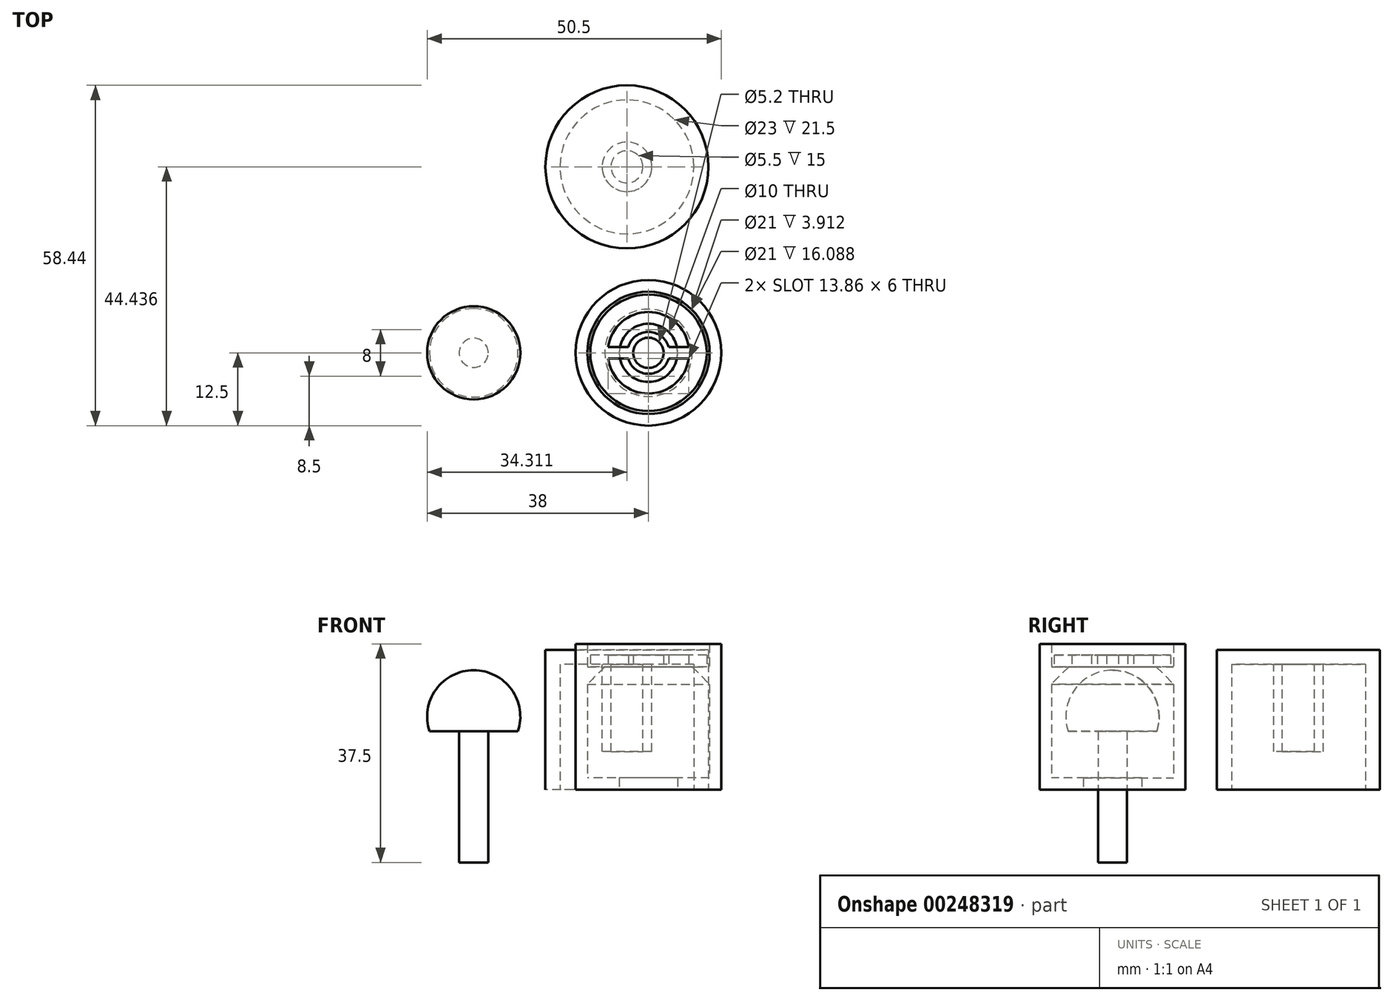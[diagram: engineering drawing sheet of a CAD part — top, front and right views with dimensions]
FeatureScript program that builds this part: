
annotation { "Feature Type Name" : "Feature", "Feature Type Description" : "" }
export const myFeature = defineFeature(function(context is Context, id is Id, definition is map)
    precondition{}
    {
        {
            var Q0;
            Q0=qCreatedBy(makeId("Top.planeOp"),FACE);
            var sketch = newSketch(context, id + "F0", { "sketchPlane" : qUnion([Q0])});
            skCircle(sketch, "E0", {"center": v(0, 0) * mm, "radius": 2.5 * mm});
            skSolve(sketch);
        }
        {
            var Q0;
            Q0=makeQuery(id+"F0.imprint","IMPRINT",FACE,{"disambiguationData":[TD([[makeQuery(id+"F0.imprint","IMPRINT",EDGE,{"derivedFrom":sQuery(id+"F0.wireOp",EDGE,"E0")}),1.0]])]});
            extrude(context, id + "F1", {"entities" : qUnion([Q0]), "endBound" : BoundingType.SYMMETRIC, "depth" : 25 * mm});
        }
        {
            var Q0;
            Q0=qCreatedBy(makeId("Right.planeOp"),FACE);
            var sketch = newSketch(context, id + "F2", { "sketchPlane" : qUnion([Q0])});
            skArc(sketch, "E1", {"start": v(7.6, 10) * mm, "mid": v(0, 20.5) * mm, "end": v(-7.6, 10) * mm});
            skLineSegment(sketch, "E2", {"start": v(7.6, 10) * mm, "end": v(-7.6, 10) * mm});
            skLineSegment(sketch, "E3", {"start": v(0, 10) * mm, "end": v(0, 20.5) * mm});
            skSolve(sketch);
        }
        {
            var Q0;
            {var subQ3=sQuery(id+"F2.wireOp",EDGE,"E3");Q0=makeQuery(id+"F2.imprint","IMPRINT",FACE,{"disambiguationData":[TD([[makeQuery(id+"F2.imprint","IMPRINT",EDGE,{"derivedFrom":subQ3}),-1.0]])]});}
            var Q1;
            Q1=sQuery(id+"F2.wireOp",EDGE,"E3");
            revolve(context, id + "F3", {"operationType" : NewBodyOperationType.ADD, "entities" : qUnion([Q0]), "axis" : qUnion([Q1]), "revolveType" : RevolveType.FULL});
        }
        {
            var Q0;
            Q0=qCreatedBy(makeId("Top.planeOp"),FACE);
            var sketch = newSketch(context, id + "F4", { "sketchPlane" : qUnion([Q0])});
            skCircle(sketch, "E4", {"center": v(30, 0) * mm, "radius": 5 * mm});
            skCircle(sketch, "E5", {"center": v(30, 0) * mm, "radius": 12.5 * mm});
            skSolve(sketch);
        }
        {
            var Q0;
            Q0=makeQuery(id+"F4.imprint","IMPRINT",FACE,{"disambiguationData":[TD([[makeQuery(id+"F4.imprint","IMPRINT",EDGE,{"derivedFrom":sQuery(id+"F4.wireOp",EDGE,"E4")}),-1.0]])]});
            extrude(context, id + "F5", {"entities" : qUnion([Q0]), "depth" : 2 * mm});
        }
        {
            var Q0;
            Q0=qCreatedBy(makeId("Front.planeOp"),FACE);
            var sketch = newSketch(context, id + "F6", { "sketchPlane" : qUnion([Q0])});
            skLineSegment(sketch, "E6.bottom", {"start": v(40.5, 0) * mm, "end": v(42.5, 0) * mm});
            skLineSegment(sketch, "E6.top", {"start": v(40.5, 25) * mm, "end": v(42.5, 25) * mm});
            skLineSegment(sketch, "E6.left", {"start": v(42.5, 0) * mm, "end": v(42.5, 25) * mm});
            skLineSegment(sketch, "E6.right", {"start": v(40.5, 0) * mm, "end": v(40.5, 25) * mm});
            skLineSegment(sketch, "E7", {"start": v(40.5, 18.09) * mm, "end": v(37.5, 21.09) * mm});
            skLineSegment(sketch, "E8", {"start": v(37.5, 21.09) * mm, "end": v(40.5, 21.09) * mm});
            skLineSegment(sketch, "E9", {"start": v(30, 0) * mm, "end": v(30, 27.95) * mm});
            skSolve(sketch);
        }
        {
            var Q0;
            {var subQ1=sQuery(id+"F6.wireOp",EDGE,"E6.bottom");Q0=makeQuery(id+"F6.imprint","IMPRINT",FACE,{"disambiguationData":[TD([[makeQuery(id+"F6.imprint","IMPRINT",EDGE,{"derivedFrom":subQ1}),1.0]])]});}
            var Q1;
            {var subQ0=sQuery(id+"F6.wireOp",EDGE,"E7");Q1=makeQuery(id+"F6.imprint","IMPRINT",FACE,{"disambiguationData":[TD([[makeQuery(id+"F6.imprint","IMPRINT",EDGE,{"derivedFrom":subQ0}),-1.0]])]});}
            var Q2;
            Q2=sQuery(id+"F6.wireOp",EDGE,"E9");
            revolve(context, id + "F7", {"operationType" : NewBodyOperationType.ADD, "entities" : qUnion([Q0, Q1]), "axis" : qUnion([Q2]), "revolveType" : RevolveType.FULL});
        }
        {
            var Q0;
            Q0=makeQuery(id+"F7.opRevolve","SWEPT_FACE",FACE,{"disambiguationData":[OSD([sQuery(id+"F6.wireOp",EDGE,"E8")])]});
            var sketch = newSketch(context, id + "F8", { "sketchPlane" : qUnion([Q0])});
            skCircle(sketch, "E10", {"center": v(30, 0) * mm, "radius": 7 * mm});
            skLineSegment(sketch, "E11", {"start": v(23.07, 1) * mm, "end": v(27.6, 1) * mm});
            skCircle(sketch, "E12", {"center": v(30, 0) * mm, "radius": 2.6 * mm});
            skCircle(sketch, "E13", {"center": v(30, 0) * mm, "radius": 3.6 * mm});
            skLineSegment(sketch, "E14", {"start": v(23, 0) * mm, "end": v(30, 0) * mm});
            skLineSegment(sketch, "E15.MirrorCS", {"start": v(23.07, -1) * mm, "end": v(27.6, -1) * mm});
            skLineSegment(sketch, "E16", {"start": v(30, 0) * mm, "end": v(30, 7) * mm});
            skLineSegment(sketch, "E17.MirrorCS", {"start": v(36.93, 1) * mm, "end": v(32.4, 1) * mm});
            skLineSegment(sketch, "E18.MirrorCS", {"start": v(36.93, -1) * mm, "end": v(32.4, -1) * mm});
            skCircle(sketch, "E19", {"center": v(30, 0) * mm, "radius": 10 * mm});
            skSolve(sketch);
        }
        {
            var Q0;
            {var subQ0=sQuery(id+"F8.wireOp",EDGE,"E12");var subQ1=sQuery(id+"F8.wireOp",EDGE,"E11");var subQ2=makeQuery(id+"F8.imprint","INTERSECT",VERTEX,{"derivedFrom":[subQ1,subQ0]});Q0=makeQuery(id+"F8.imprint","IMPRINT",FACE,{"disambiguationData":[TD([[makeQuery(id+"F8.imprint","IMPRINT",EDGE,{"disambiguationData":[TD([[subQ2,1.0]])],"derivedFrom":subQ1}),1.0]])]});}
            var Q1;
            {var subQ0=sQuery(id+"F8.wireOp",EDGE,"E17.MirrorCS");var subQ1=sQuery(id+"F8.wireOp",EDGE,"E12");var subQ2=makeQuery(id+"F8.imprint","INTERSECT",VERTEX,{"derivedFrom":[subQ1,subQ0]});Q1=makeQuery(id+"F8.imprint","IMPRINT",FACE,{"disambiguationData":[TD([[makeQuery(id+"F8.imprint","IMPRINT",EDGE,{"disambiguationData":[TD([[subQ2,-1.0]])],"derivedFrom":subQ1}),-1.0]])]});}
            var Q2;
            {var subQ0=sQuery(id+"F8.wireOp",EDGE,"E15.MirrorCS");var subQ1=sQuery(id+"F8.wireOp",EDGE,"E12");var subQ2=makeQuery(id+"F8.imprint","INTERSECT",VERTEX,{"derivedFrom":[subQ1,subQ0]});Q2=makeQuery(id+"F8.imprint","IMPRINT",FACE,{"disambiguationData":[TD([[makeQuery(id+"F8.imprint","IMPRINT",EDGE,{"disambiguationData":[TD([[subQ2,-1.0]])],"derivedFrom":subQ1}),-1.0]])]});}
            var Q3;
            {var subQ0=sQuery(id+"F8.wireOp",EDGE,"E17.MirrorCS");var subQ1=sQuery(id+"F8.wireOp",EDGE,"E12");var subQ2=makeQuery(id+"F8.imprint","INTERSECT",VERTEX,{"derivedFrom":[subQ1,subQ0]});Q3=makeQuery(id+"F8.imprint","IMPRINT",FACE,{"disambiguationData":[TD([[makeQuery(id+"F8.imprint","IMPRINT",EDGE,{"disambiguationData":[TD([[subQ2,1.0]])],"derivedFrom":subQ1}),-1.0]])]});}
            var Q4;
            {var subQ0=sQuery(id+"F8.wireOp",EDGE,"E14");var subQ1=sQuery(id+"F8.wireOp",EDGE,"E13");var subQ2=makeQuery(id+"F8.imprint","INTERSECT",VERTEX,{"derivedFrom":[subQ1,subQ0]});Q4=makeQuery(id+"F8.imprint","IMPRINT",FACE,{"disambiguationData":[TD([[makeQuery(id+"F8.imprint","IMPRINT",EDGE,{"disambiguationData":[TD([[subQ2,-1.0]])],"derivedFrom":subQ1}),-1.0]])]});}
            var Q5;
            {var subQ0=sQuery(id+"F8.wireOp",EDGE,"E13");var subQ1=sQuery(id+"F8.wireOp",EDGE,"E11");var subQ2=makeQuery(id+"F8.imprint","INTERSECT",VERTEX,{"derivedFrom":[subQ1,subQ0]});Q5=makeQuery(id+"F8.imprint","IMPRINT",FACE,{"disambiguationData":[TD([[makeQuery(id+"F8.imprint","IMPRINT",EDGE,{"disambiguationData":[TD([[subQ2,-1.0]])],"derivedFrom":subQ0}),-1.0]])]});}
            var Q6;
            {var subQ0=sQuery(id+"F8.wireOp",EDGE,"E12");var subQ1=sQuery(id+"F8.wireOp",EDGE,"E11");var subQ2=makeQuery(id+"F8.imprint","INTERSECT",VERTEX,{"derivedFrom":[subQ1,subQ0]});Q6=makeQuery(id+"F8.imprint","IMPRINT",FACE,{"disambiguationData":[TD([[makeQuery(id+"F8.imprint","IMPRINT",EDGE,{"disambiguationData":[TD([[subQ2,1.0]])],"derivedFrom":subQ1}),-1.0]])]});}
            var Q7;
            {var subQ0=sQuery(id+"F8.wireOp",EDGE,"E15.MirrorCS");var subQ1=sQuery(id+"F8.wireOp",EDGE,"E12");var subQ2=makeQuery(id+"F8.imprint","INTERSECT",VERTEX,{"derivedFrom":[subQ1,subQ0]});Q7=makeQuery(id+"F8.imprint","IMPRINT",FACE,{"disambiguationData":[TD([[makeQuery(id+"F8.imprint","IMPRINT",EDGE,{"disambiguationData":[TD([[subQ2,1.0]])],"derivedFrom":subQ1}),-1.0]])]});}
            var Q8;
            {var subQ0=sQuery(id+"F8.wireOp",EDGE,"E17.MirrorCS");var subQ1=sQuery(id+"F8.wireOp",EDGE,"E10");var subQ2=makeQuery(id+"F8.imprint","INTERSECT",VERTEX,{"derivedFrom":[subQ1,subQ0]});Q8=makeQuery(id+"F8.imprint","IMPRINT",FACE,{"disambiguationData":[TD([[makeQuery(id+"F8.imprint","IMPRINT",EDGE,{"disambiguationData":[TD([[subQ2,1.0]])],"derivedFrom":subQ1}),1.0]])]});}
            var Q9;
            {var subQ0=sQuery(id+"F8.wireOp",EDGE,"E14");var subQ1=sQuery(id+"F8.wireOp",EDGE,"E10");var subQ2=makeQuery(id+"F8.imprint","INTERSECT",VERTEX,{"derivedFrom":[subQ1,subQ0]});Q9=makeQuery(id+"F8.imprint","IMPRINT",FACE,{"disambiguationData":[TD([[makeQuery(id+"F8.imprint","IMPRINT",EDGE,{"disambiguationData":[TD([[subQ2,-1.0]])],"derivedFrom":subQ1}),1.0]])]});}
            var Q10;
            {var subQ0=sQuery(id+"F8.wireOp",EDGE,"E11");var subQ1=sQuery(id+"F8.wireOp",EDGE,"E10");var subQ2=makeQuery(id+"F8.imprint","INTERSECT",VERTEX,{"derivedFrom":[subQ1,subQ0]});Q10=makeQuery(id+"F8.imprint","IMPRINT",FACE,{"disambiguationData":[TD([[makeQuery(id+"F8.imprint","IMPRINT",EDGE,{"disambiguationData":[TD([[subQ2,-1.0]])],"derivedFrom":subQ1}),1.0]])]});}
            var Q11;
            {var subQ0=sQuery(id+"F8.wireOp",EDGE,"E17.MirrorCS");var subQ1=sQuery(id+"F8.wireOp",EDGE,"E13");var subQ2=makeQuery(id+"F8.imprint","INTERSECT",VERTEX,{"derivedFrom":[subQ1,subQ0]});Q11=makeQuery(id+"F8.imprint","IMPRINT",FACE,{"disambiguationData":[TD([[makeQuery(id+"F8.imprint","IMPRINT",EDGE,{"disambiguationData":[TD([[subQ2,1.0]])],"derivedFrom":subQ1}),-1.0]])]});}
            var Q12;
            Q12=makeQuery(id+"F8.imprint","IMPRINT",FACE,{"disambiguationData":[TD([[makeQuery(id+"F8.imprint","IMPRINT",EDGE,{"derivedFrom":sQuery(id+"F8.wireOp",EDGE,"E19")}),1.0]])]});
            var Q13;
            Q13=makeQuery(id+"F8.imprint","IMPRINT",FACE,{"disambiguationData":[TD([[makeQuery(id+"F8.imprint","IMPRINT",EDGE,{"derivedFrom":makeQuery(id+"F7.opRevolve","SWEPT_EDGE",EDGE,{"disambiguationData":[OSD([sQuery(id+"F6.wireOp",EDGE,"E7"),sQuery(id+"F6.wireOp",EDGE,"E8")])]})}),-1.0]])]});
            extrude(context, id + "F9", {"entities" : qUnion([Q0, Q1, Q2, Q3, Q4, Q5, Q6, Q7, Q8, Q9, Q10, Q11, Q12, Q13]), "depth" : 2 * mm});
        }
        {
            var Q0;
            Q0=qCreatedBy(makeId("Top.planeOp"),FACE);
            var sketch = newSketch(context, id + "F10", { "sketchPlane" : qUnion([Q0])});
            skCircle(sketch, "E20", {"center": v(26.31, 31.94) * mm, "radius": 14 * mm});
            skSolve(sketch);
        }
        {
            var Q0;
            Q0=makeQuery(id+"F10.imprint","IMPRINT",FACE,{"disambiguationData":[TD([[makeQuery(id+"F10.imprint","IMPRINT",EDGE,{"derivedFrom":sQuery(id+"F10.wireOp",EDGE,"E20")}),1.0]])]});
            extrude(context, id + "F11", {"entities" : qUnion([Q0]), "depth" : 24 * mm});
        }
        {
            var Q0;
            Q0=makeQuery(id+"F11.opExtrude","CAP_FACE",FACE,{"disambiguationData":[OSD([sQuery(id+"F10.wireOp",EDGE,"E20")])],"isStart":true});
            shell(context, id + "F12", {"entities" : qUnion([Q0]), "thickness" : 2.5 * mm});
        }
        {
            var Q0;
            {var subQ0=sQuery(id+"F10.wireOp",EDGE,"E20");Q0=makeQuery(id+"F12.opShell","OFFSET_FACE",FACE,{"disambiguationData":[OSD([subQ0]),TDD([makeQuery(id+"F11.opExtrude","CAP_FACE",FACE,{"disambiguationData":[OSD([subQ0])],"isStart":false})])]});}
            var sketch = newSketch(context, id + "F13", { "sketchPlane" : qUnion([Q0])});
            skCircle(sketch, "E21", {"center": v(26.31, -31.94) * mm, "radius": 2.75 * mm});
            skCircle(sketch, "E22", {"center": v(26.31, -31.94) * mm, "radius": 4.25 * mm});
            skSolve(sketch);
        }
        {
            var Q0;
            Q0 = qSketchRegion(id + "F13", true);
            extrude(context, id + "F14", {"entities" : qUnion([Q0]), "operationType" : NewBodyOperationType.ADD, "depth" : 15 * mm});
        }
    });
